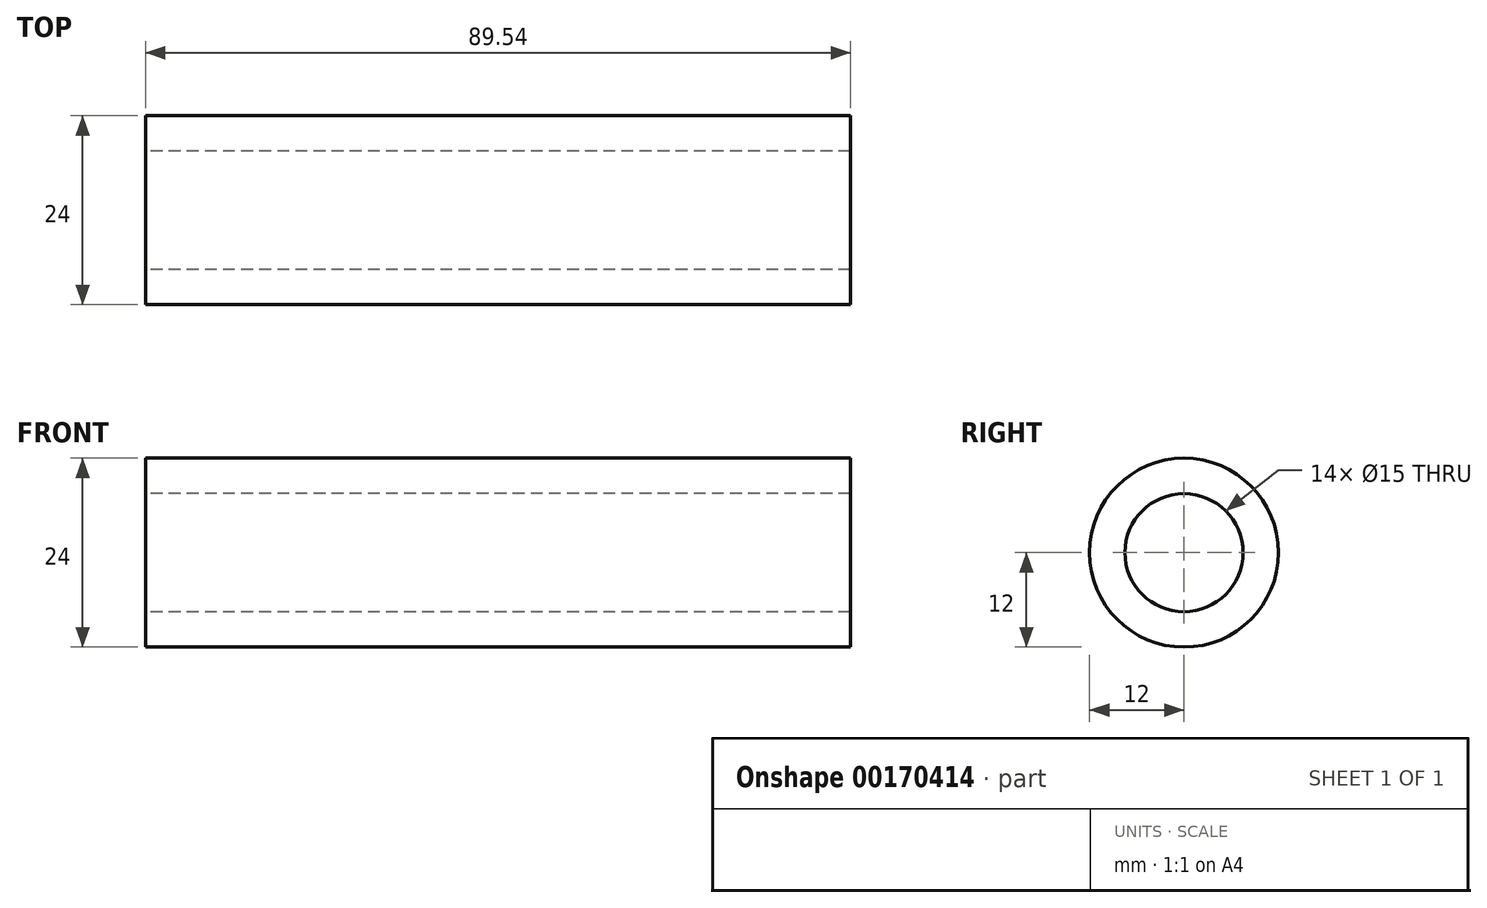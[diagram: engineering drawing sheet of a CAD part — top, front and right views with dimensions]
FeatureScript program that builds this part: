
annotation { "Feature Type Name" : "Feature", "Feature Type Description" : "" }
export const myFeature = defineFeature(function(context is Context, id is Id, definition is map)
    precondition{}
    {
        {
            var Q0;
            Q0=qCreatedBy(makeId("Right.planeOp"),FACE);
            var sketch = newSketch(context, id + "F0", { "sketchPlane" : qUnion([Q0])});
            skCircle(sketch, "E0", {"center": v(0, 0) * mm, "radius": 12 * mm});
            skCircle(sketch, "E1", {"center": v(0, 0) * mm, "radius": 7.5 * mm});
            skSolve(sketch);
        }
        {
            var Q0;
            Q0 = qSketchRegion(id + "F0", true);
            extrude(context, id + "F1", {"entities" : qUnion([Q0]), "depth" : 89.53 * mm});
        }
    });
